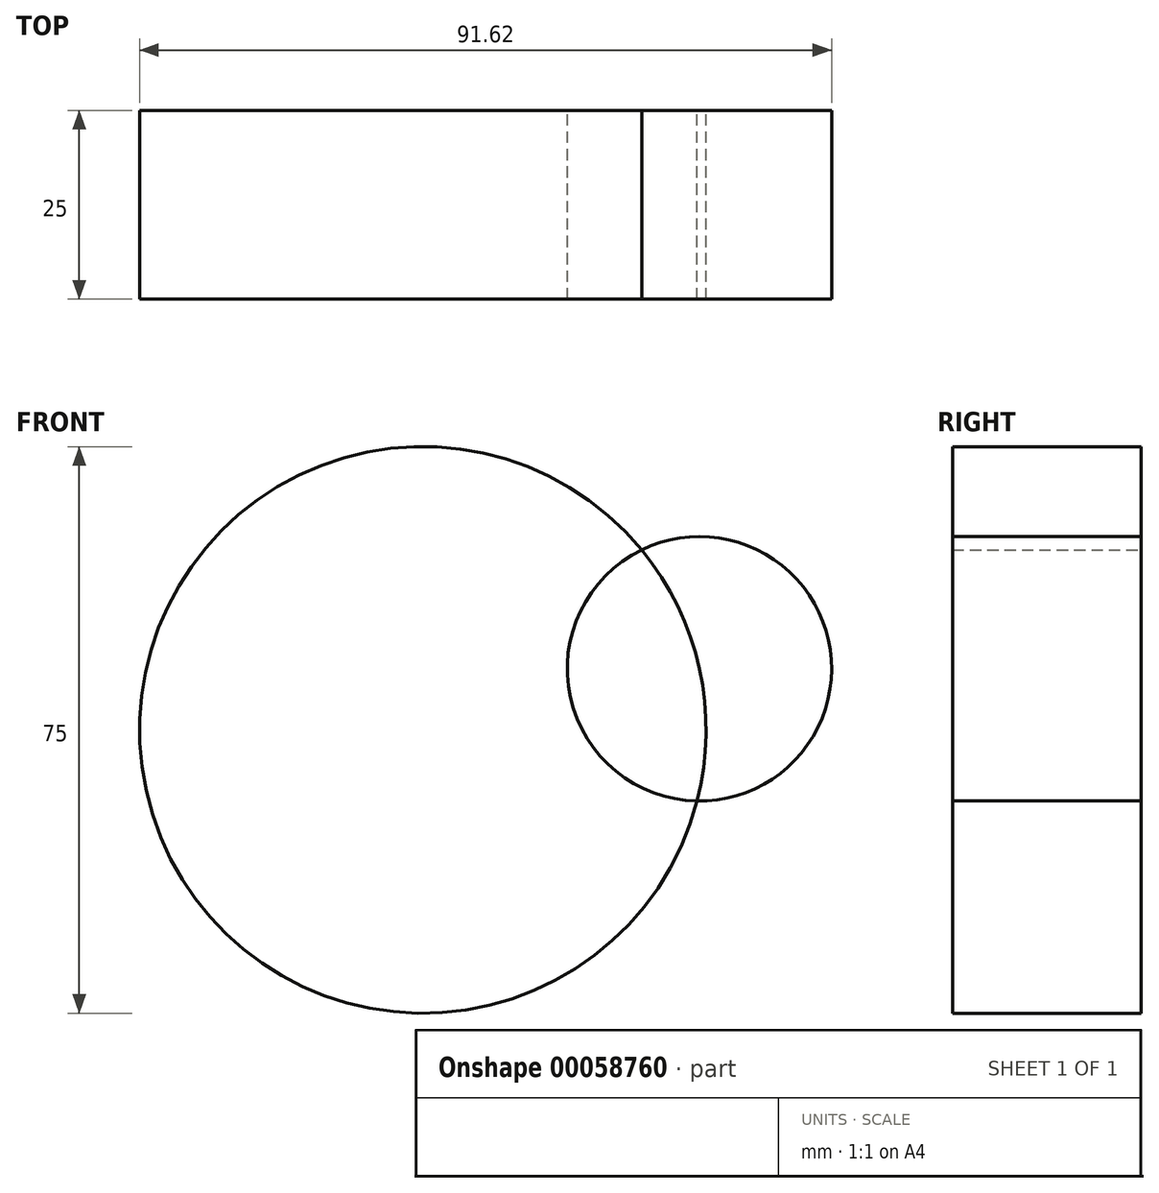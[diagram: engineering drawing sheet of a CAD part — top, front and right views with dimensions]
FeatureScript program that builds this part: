
annotation { "Feature Type Name" : "Feature", "Feature Type Description" : "" }
export const myFeature = defineFeature(function(context is Context, id is Id, definition is map)
    precondition{}
    {
        {
            var Q0;
            Q0=qCreatedBy(makeId("Front.planeOp"),FACE);
            var sketch = newSketch(context, id + "F0", { "sketchPlane" : qUnion([Q0])});
            skCircle(sketch, "E0", {"center": v(0, 0) * mm, "radius": 37.5 * mm});
            skCircle(sketch, "E1", {"center": v(36.62, 8.09) * mm, "radius": 17.5 * mm});
            skSolve(sketch);
        }
        {
            var Q0;
            {var subQ0=sQuery(id+"F0.wireOp",EDGE,"E1");var subQ1=sQuery(id+"F0.wireOp",EDGE,"E0");var subQ2=makeQuery(id+"F0.imprint","INTERSECT",VERTEX,{"disambiguationData":[OD(0.0)],"derivedFrom":[subQ1,subQ0]});Q0=makeQuery(id+"F0.imprint","IMPRINT",FACE,{"disambiguationData":[TD([[makeQuery(id+"F0.imprint","IMPRINT",EDGE,{"disambiguationData":[TD([[subQ2,1.0]])],"derivedFrom":subQ1}),1.0]])]});}
            var Q1;
            {var subQ0=sQuery(id+"F0.wireOp",EDGE,"E1");var subQ1=sQuery(id+"F0.wireOp",EDGE,"E0");var subQ2=makeQuery(id+"F0.imprint","INTERSECT",VERTEX,{"disambiguationData":[OD(0.0)],"derivedFrom":[subQ1,subQ0]});Q1=makeQuery(id+"F0.imprint","IMPRINT",FACE,{"disambiguationData":[TD([[makeQuery(id+"F0.imprint","IMPRINT",EDGE,{"disambiguationData":[TD([[subQ2,-1.0]])],"derivedFrom":subQ1}),-1.0]])]});}
            extrude(context, id + "F1", {"entities" : qUnion([Q0, Q1]), "depth" : 25 * mm});
        }
    });
